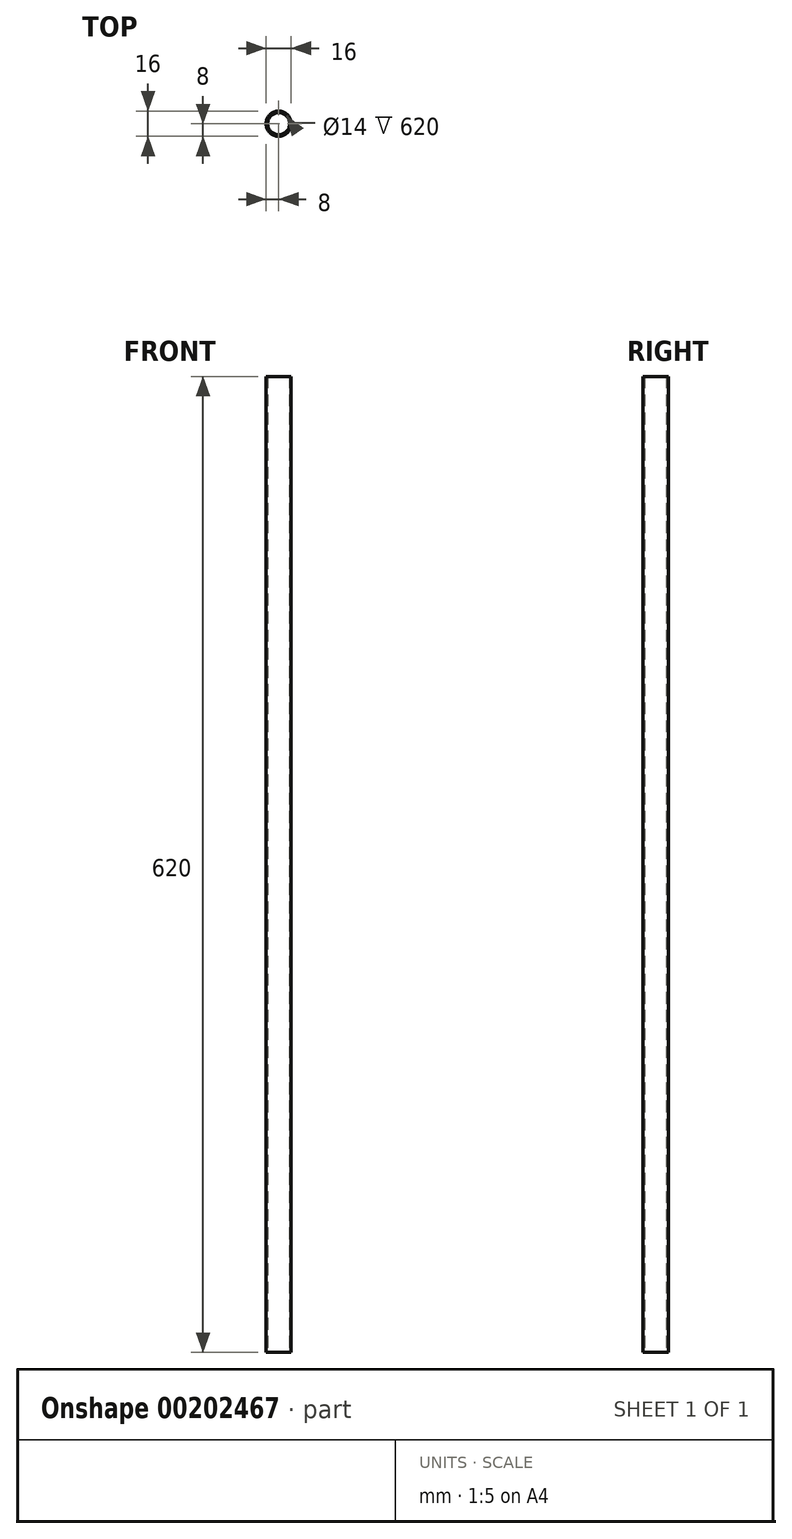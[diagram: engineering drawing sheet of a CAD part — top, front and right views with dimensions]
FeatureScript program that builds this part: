
annotation { "Feature Type Name" : "Feature", "Feature Type Description" : "" }
export const myFeature = defineFeature(function(context is Context, id is Id, definition is map)
    precondition{}
    {
        {
            var Q0;
            Q0=qCreatedBy(makeId("Top.planeOp"),FACE);
            var sketch = newSketch(context, id + "F0", { "sketchPlane" : qUnion([Q0])});
            skCircle(sketch, "E0", {"center": v(0, 0) * mm, "radius": 8 * mm});
            skCircle(sketch, "E1.0", {"center": v(0, 0) * mm, "radius": 7 * mm});
            skSolve(sketch);
        }
        {
            var Q0;
            Q0=qSketchRegion(id+"F0",true);
            extrude(context, id + "F1", {"entities" : qUnion([Q0]), "depth" : 620 * mm});
        }
    });
